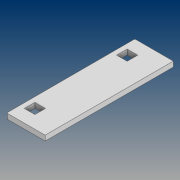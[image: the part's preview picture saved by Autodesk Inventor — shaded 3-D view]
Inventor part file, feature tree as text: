
AUTODESK INVENTOR PART (.ipt)
format: ipt  version: 2021 (Build 250183000, 183)  size: 98,304 bytes
history: native  units: mm
features: extrude x1, fillet x1, sketch x1
ambient origin geometry x8: Origin, YZ Plane, XZ Plane, XY Plane, X Axis, Y Axis, Z Axis, Center Point
bodies: Solid1 (feature_tree)
feature tree (3):
  extrude  "Extrusion1"  Depth=2.0mm
  fillet  "Fillet1"  Radius=180.0mm
  sketch  "Sketch1"  dims[d0=250.0mm d1=40.0mm d2=180.0mm d3=20.5mm d4=35.0mm d5=10.0mm d6=0.0mm d7=2.0mm]
